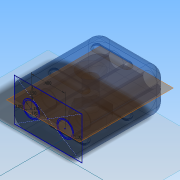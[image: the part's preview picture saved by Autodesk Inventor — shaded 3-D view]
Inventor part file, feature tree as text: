
AUTODESK INVENTOR PART (.ipt)
format: ipt  version: 2014 SP2 (Build 180246200, 246)  size: 257,024 bytes
history: native  units: in
note: dims shown in document units (in); Inventor stores cm internally (conversion verified against a paired STEP export)
features: sketch x5, extrude x5, fillet x3, projected_geometry x2, hole x1, pattern_linear x1, other x1, mirror x1, split x1
ambient origin geometry x8: Origin, YZ Plane, XZ Plane, XY Plane, X Axis, Y Axis, Z Axis, Center Point
bodies: Solid1 (feature_tree), Solid2 (feature_tree), Solid3 (feature_tree)
feature tree (20):
  sketch  "Sketch1"  dims[d0=0.4in d1=0.196in]
  extrude  "Base"  Depth=0.196in
  extrude  "Wire holes"  Depth=0.1in
  extrude  "Bullet holes"  Depth=0.17in
  hole  "Hole1"  [1 undecoded]
  extrude  "Extrusion5"  Depth=1.0in
  extrude  "Nub"  Depth=1.0in
  fillet  "Nub Fillet"  Radius=0.1in
  pattern_linear  "Nub Rectangular Pattern1"  Spacing1=0.25in  [1 undecoded]
  fillet  "Fillet1"  Radius=0.22in
  fillet  "Fillet2"  Radius=0.05in
  other  "Midplane"
  mirror  "Nub Mirror1"
  split  "Split1"
  sketch  "Sketch5"  dims[d10=0.21in d11=0.0in d12=0.125in d13=0.125in d14=0.1in d15=0.25in d16=0.22in d17=0.05in d18=0.0in d19=0.05in d20=1.1811in d22=0.25in d23=0.15in d24=0.75in d25=0.279in d26=0.0625in d27=0.5635in d28=1.0in d29=0.8108in d30=0.3325in d31=0.1094in d32=0.0in]
  sketch  "Sketch2"  dims[d2=0.15in d3=0.1in]
  projected_geometry  "Projected Loop1"
  sketch  "Sketch3"  dims[d4=0.1in d5=0.17in]
  projected_geometry  "Projected Loop2"
  sketch  "Sketch4"  dims[d6=1.0in d7=0.0in d8=1.0in d9=0.0in]
note: 2 required parameter values undecoded (feature->parameter linkage not recoverable at this tier; creation-order binding heuristic only, values carry confidence <= 0.55)
